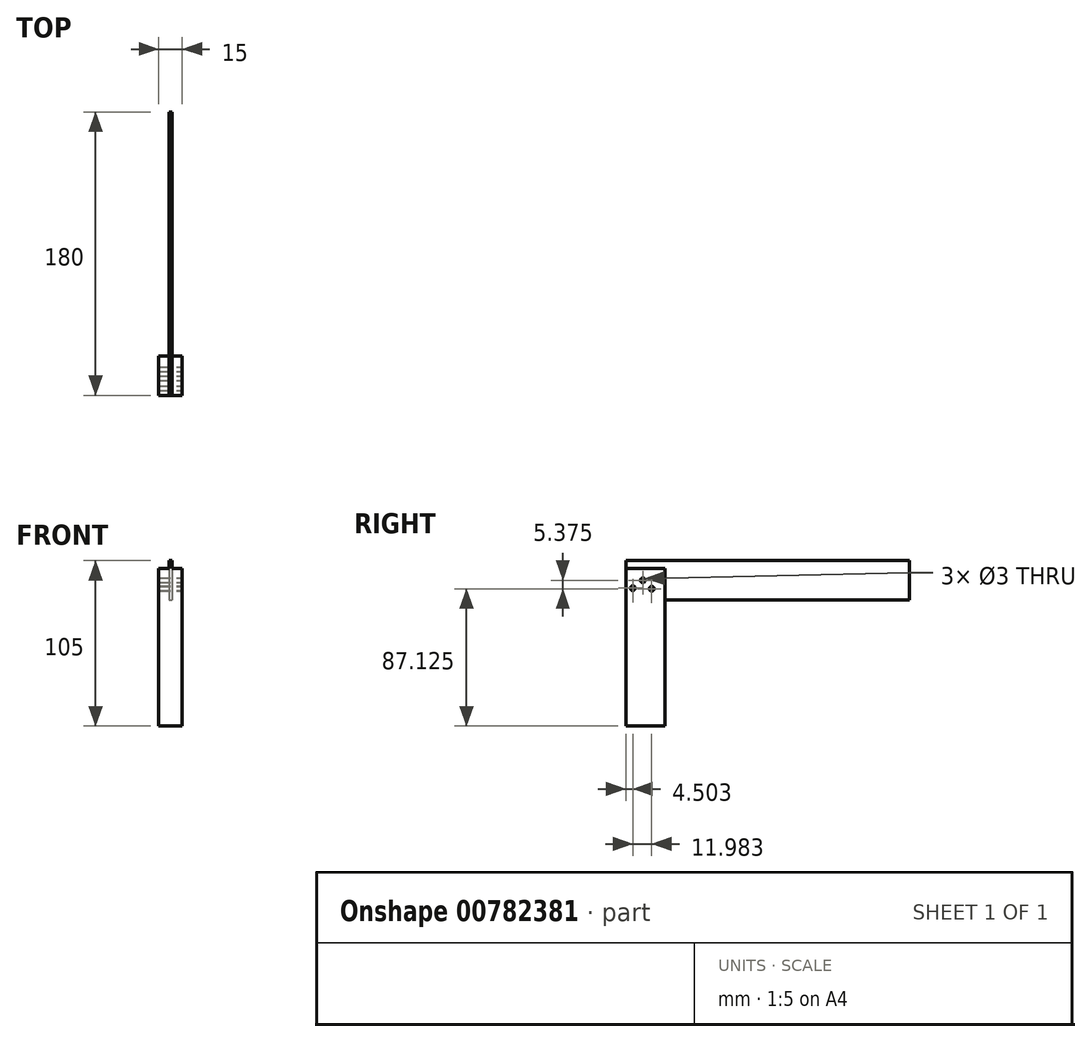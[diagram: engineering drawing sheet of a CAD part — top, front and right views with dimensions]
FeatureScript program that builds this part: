
annotation { "Feature Type Name" : "Feature", "Feature Type Description" : "" }
export const myFeature = defineFeature(function(context is Context, id is Id, definition is map)
    precondition{}
    {
        {
            var Q0;
            Q0=qCreatedBy(makeId("Front.planeOp"),FACE);
            var sketch = newSketch(context, id + "F0", { "sketchPlane" : qUnion([Q0])});
            skLineSegment(sketch, "E0.bottom", {"start": v(0, 0) * mm, "end": v(-15, 0) * mm});
            skLineSegment(sketch, "E0.top", {"start": v(0, 100) * mm, "end": v(-15, 100) * mm});
            skLineSegment(sketch, "E0.left", {"start": v(0, 0) * mm, "end": v(0, 100) * mm});
            skLineSegment(sketch, "E0.right", {"start": v(-15, 0) * mm, "end": v(-15, 100) * mm});
            skSolve(sketch);
        }
        {
            var Q0;
            Q0 = qSketchRegion(id + "F0", true);
            extrude(context, id + "F1", {"entities" : qUnion([Q0]), "depth" : 25 * mm, "offsetDistance" : 25 * mm});
        }
        {
            var Q0;
            Q0=makeQuery(id+"F1.opExtrude","CAP_FACE",FACE,{"disambiguationData":[OSD([sQuery(id+"F0.wireOp",EDGE,"E0.bottom"),sQuery(id+"F0.wireOp",EDGE,"E0.top"),sQuery(id+"F0.wireOp",EDGE,"E0.left"),sQuery(id+"F0.wireOp",EDGE,"E0.right")])],"isStart":false});
            var sketch = newSketch(context, id + "F2", { "sketchPlane" : qUnion([Q0])});
            skLineSegment(sketch, "E1.bottom", {"start": v(-8.5, 100) * mm, "end": v(-6.5, 100) * mm});
            skLineSegment(sketch, "E1.top", {"start": v(-8.5, 80) * mm, "end": v(-6.5, 80) * mm});
            skLineSegment(sketch, "E1.left", {"start": v(-8.5, 100) * mm, "end": v(-8.5, 80) * mm});
            skLineSegment(sketch, "E1.right", {"start": v(-6.5, 100) * mm, "end": v(-6.5, 80) * mm});
            skSolve(sketch);
        }
        {
            var Q0;
            Q0=makeQuery(id+"F2.imprint","IMPRINT",FACE,{"disambiguationData":[TD([[makeQuery(id+"F2.imprint","IMPRINT",EDGE,{"derivedFrom":sQuery(id+"F2.wireOp",EDGE,"E1.bottom")}),1.0]])]});
            extrude(context, id + "F3", {"entities" : qUnion([Q0]), "operationType" : NewBodyOperationType.REMOVE, "oppositeDirection" : true, "depth" : 25 * mm, "offsetDistance" : 25 * mm});
        }
        {
            var Q0;
            Q0=makeQuery(id+"F2.imprint","IMPRINT",FACE,{"disambiguationData":[TD([[makeQuery(id+"F2.imprint","IMPRINT",EDGE,{"derivedFrom":sQuery(id+"F2.wireOp",EDGE,"E1.bottom")}),1.0]])]});
            extrude(context, id + "F4", {"entities" : qUnion([Q0]), "oppositeDirection" : true, "depth" : 180 * mm, "offsetDistance" : 25 * mm});
        }
        {
            var Q0;
            Q0=makeQuery(id+"F4.opExtrude","SWEPT_FACE",FACE,{"disambiguationData":[OSD([sQuery(id+"F2.wireOp",EDGE,"E1.bottom")])]});
            extrude(context, id + "F5", {"entities" : qUnion([Q0]), "operationType" : NewBodyOperationType.ADD, "depth" : 5 * mm, "offsetDistance" : 25 * mm});
        }
        {
            var Q0;
            Q0=makeQuery(id+"F1.opExtrude","SWEPT_FACE",FACE,{"disambiguationData":[OSD([sQuery(id+"F0.wireOp",EDGE,"E0.left")])]});
            var sketch = newSketch(context, id + "F6", { "sketchPlane" : qUnion([Q0])});
            skSolve(sketch);
        }
        {
            var Q0;
            {var subQ0=sQuery(id+"F0.wireOp",EDGE,"E0.left");Q0=makeQuery(id+"F6.imprint","IMPRINT",FACE,{"disambiguationData":[TD([[makeQuery(id+"F6.imprint","IMPRINT",EDGE,{"derivedFrom":makeQuery(id+"F1.opExtrude","CAP_EDGE",EDGE,{"disambiguationData":[OSD([subQ0])],"isStart":true})}),1.0]])]});}
            var sketch = newSketch(context, id + "F7", { "sketchPlane" : qUnion([Q0])});
            skCircle(sketch, "E2", {"center": v(-14.14, 92.5) * mm, "radius": 1.5 * mm});
            skCircle(sketch, "E3", {"center": v(-20.5, 87.5) * mm, "radius": 1.5 * mm});
            skCircle(sketch, "E4", {"center": v(-8.51, 87.13) * mm, "radius": 1.5 * mm});
            skSolve(sketch);
        }
        {
            var Q0;
            Q0 = qSketchRegion(id + "F7", true);
            extrude(context, id + "F8", {"entities" : qUnion([Q0]), "operationType" : NewBodyOperationType.REMOVE, "oppositeDirection" : true, "depth" : 15 * mm, "offsetDistance" : 25 * mm});
        }
        {
            var Q0;
            {var subQ0=sQuery(id+"F0.wireOp",EDGE,"E0.left");Q0=makeQuery(id+"F6.imprint","IMPRINT",FACE,{"disambiguationData":[TD([[makeQuery(id+"F6.imprint","IMPRINT",EDGE,{"derivedFrom":makeQuery(id+"F1.opExtrude","CAP_EDGE",EDGE,{"disambiguationData":[OSD([subQ0])],"isStart":true})}),1.0]])]});}
            var sketch = newSketch(context, id + "F9", { "sketchPlane" : qUnion([Q0])});
            skCircle(sketch, "E5", {"center": v(-14.14, 92.5) * mm, "radius": 1.5 * mm});
            skCircle(sketch, "E6", {"center": v(-20.5, 87.5) * mm, "radius": 1.5 * mm});
            skCircle(sketch, "E7", {"center": v(-8.51, 87.13) * mm, "radius": 1.5 * mm});
            skSolve(sketch);
        }
        {
            var Q0;
            Q0 = qSketchRegion(id + "F9", true);
            extrude(context, id + "F10", {"entities" : qUnion([Q0]), "oppositeDirection" : true, "depth" : 15 * mm, "offsetDistance" : 25 * mm});
        }
    });
